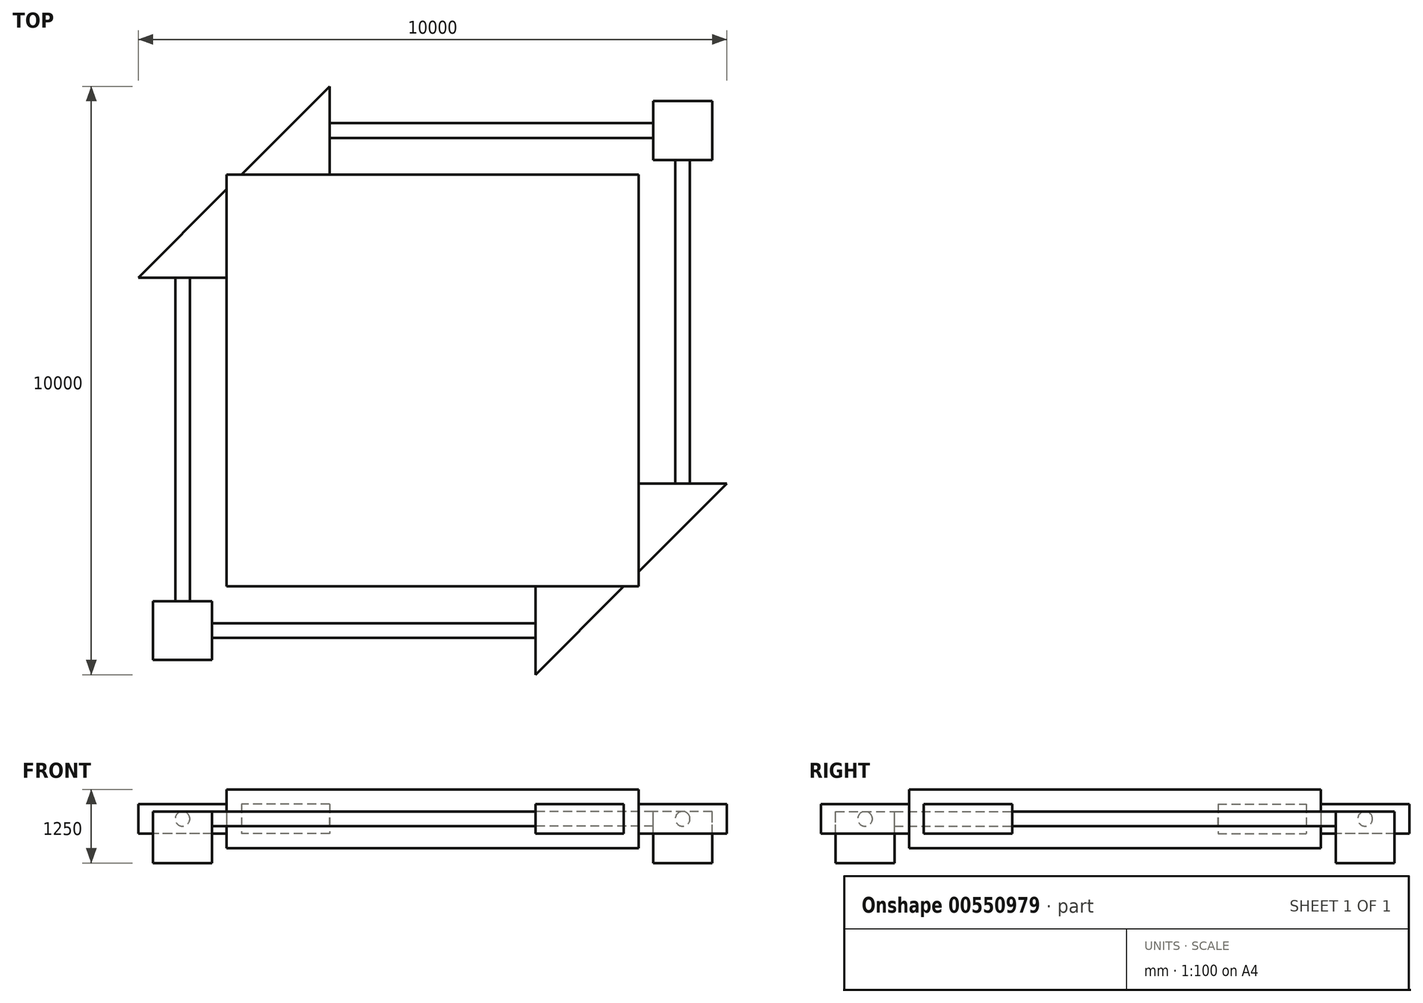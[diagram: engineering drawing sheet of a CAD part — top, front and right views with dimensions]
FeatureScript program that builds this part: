
annotation { "Feature Type Name" : "Feature", "Feature Type Description" : "" }
export const myFeature = defineFeature(function(context is Context, id is Id, definition is map)
    precondition{}
    {
        {
            var Q0;
            Q0=qCreatedBy(makeId("Top.planeOp"),FACE);
            var sketch = newSketch(context, id + "F0", { "sketchPlane" : qUnion([Q0])});
            skLineSegment(sketch, "E0.bottom", {"start": v(3500, -3500) * mm, "end": v(-3500, -3500) * mm});
            skLineSegment(sketch, "E0.top", {"start": v(3500, 3500) * mm, "end": v(-3500, 3500) * mm});
            skLineSegment(sketch, "E0.left", {"start": v(3500, -3500) * mm, "end": v(3500, 3500) * mm});
            skLineSegment(sketch, "E0.right", {"start": v(-3500, -3500) * mm, "end": v(-3500, 3500) * mm});
            skPoint(sketch, "E0.middle", {"position": v(0, 0) * mm});
            skLineSegment(sketch, "E1", {"start": v(0, 3500) * mm, "end": v(0, -3500) * mm, "construction": true});
            skLineSegment(sketch, "E2", {"start": v(-3500, 0) * mm, "end": v(3500, 0) * mm, "construction": true});
            skSolve(sketch);
        }
        {
            var Q0;
            Q0=makeQuery(id+"F0.imprint","IMPRINT",FACE,{"disambiguationData":[TD([[makeQuery(id+"F0.imprint","IMPRINT",EDGE,{"derivedFrom":sQuery(id+"F0.wireOp",EDGE,"E0.bottom")}),-1.0]])]});
            extrude(context, id + "F1", {"entities" : qUnion([Q0]), "depth" : 1000 * mm, "offsetDistance" : 25 * mm});
        }
        {
            var Q0;
            Q0=makeQuery(id+"F1.opExtrude","CAP_FACE",FACE,{"disambiguationData":[OSD([sQuery(id+"F0.wireOp",EDGE,"E0.bottom"),sQuery(id+"F0.wireOp",EDGE,"E0.top"),sQuery(id+"F0.wireOp",EDGE,"E0.left"),sQuery(id+"F0.wireOp",EDGE,"E0.right")])],"isStart":false});
            cPlane(context, id + "F2", {"entities" : qUnion([Q0]), "cplaneType" : CPlaneType.OFFSET, "offset" : 500 * mm, "oppositeDirection" : true, "width" : 150 * mm, "height" : 150 * mm});
        }
        {
            var Q0;
            Q0=qCreatedBy(id+"F2.planeOp",FACE);
            var sketch = newSketch(context, id + "F3", { "sketchPlane" : qUnion([Q0])});
            skLineSegment(sketch, "E3.0", {"start": v(3500, -3500) * mm, "end": v(-3500, -3500) * mm});
            skLineSegment(sketch, "E3.1", {"start": v(-3500, -3500) * mm, "end": v(-3500, 3500) * mm});
            skLineSegment(sketch, "E3.2", {"start": v(3500, 3500) * mm, "end": v(-3500, 3500) * mm});
            skLineSegment(sketch, "E3.3", {"start": v(3500, -3500) * mm, "end": v(3500, 3500) * mm});
            skLineSegment(sketch, "E4", {"start": v(-3500, 1750) * mm, "end": v(-5000, 1750) * mm});
            skLineSegment(sketch, "E5", {"start": v(-4250, 1750) * mm, "end": v(-4250, -4250) * mm});
            skLineSegment(sketch, "E6.bottom", {"start": v(-3750, -4750) * mm, "end": v(-4750, -4750) * mm});
            skLineSegment(sketch, "E6.top", {"start": v(-3750, -3750) * mm, "end": v(-4750, -3750) * mm});
            skLineSegment(sketch, "E6.left", {"start": v(-3750, -4750) * mm, "end": v(-3750, -3750) * mm});
            skLineSegment(sketch, "E6.right", {"start": v(-4750, -4750) * mm, "end": v(-4750, -3750) * mm});
            skPoint(sketch, "E6.middle", {"position": v(-4250, -4250) * mm});
            skPoint(sketch, "E7.orphan", {"position": v(-3500, 3250) * mm});
            skLineSegment(sketch, "E8", {"start": v(-1750, 5000) * mm, "end": v(-1750, 3500) * mm});
            skLineSegment(sketch, "E9", {"start": v(-3500, 3250) * mm, "end": v(-5000, 1750) * mm});
            skLineSegment(sketch, "E10", {"start": v(-1750, 5000) * mm, "end": v(-3250, 3500) * mm});
            skLineSegment(sketch, "E11", {"start": v(-1750, 4250) * mm, "end": v(4250, 4250) * mm});
            skLineSegment(sketch, "E12.bottom", {"start": v(4750, 3750) * mm, "end": v(3750, 3750) * mm});
            skLineSegment(sketch, "E12.top", {"start": v(4750, 4750) * mm, "end": v(3750, 4750) * mm});
            skLineSegment(sketch, "E12.left", {"start": v(4750, 3750) * mm, "end": v(4750, 4750) * mm});
            skLineSegment(sketch, "E12.right", {"start": v(3750, 3750) * mm, "end": v(3750, 4750) * mm});
            skPoint(sketch, "E12.middle", {"position": v(4250, 4250) * mm});
            skSolve(sketch);
        }
        {
            var Q0;
            {var subQ3=sQuery(id+"F3.wireOp",EDGE,"E9");Q0=makeQuery(id+"F3.imprint","IMPRINT",FACE,{"disambiguationData":[TD([[makeQuery(id+"F3.imprint","IMPRINT",EDGE,{"derivedFrom":subQ3}),1.0]])]});}
            var Q1;
            {var subQ3=sQuery(id+"F3.wireOp",EDGE,"E10");Q1=makeQuery(id+"F3.imprint","IMPRINT",FACE,{"disambiguationData":[TD([[makeQuery(id+"F3.imprint","IMPRINT",EDGE,{"derivedFrom":subQ3}),1.0]])]});}
            extrude(context, id + "F4", {"entities" : qUnion([Q0, Q1]), "endBound" : BoundingType.SYMMETRIC, "depth" : 500 * mm, "offsetDistance" : 25 * mm});
        }
        {
            var Q0;
            Q0=makeQuery(id+"F3.imprint","IMPRINT",FACE,{"disambiguationData":[TD([[makeQuery(id+"F3.imprint","IMPRINT",EDGE,{"derivedFrom":sQuery(id+"F3.wireOp",EDGE,"E6.bottom")}),-1.0]])]});
            var Q1;
            {var subQ1=sQuery(id+"F3.wireOp",EDGE,"E12.bottom");Q1=makeQuery(id+"F3.imprint","IMPRINT",FACE,{"disambiguationData":[TD([[makeQuery(id+"F3.imprint","IMPRINT",EDGE,{"derivedFrom":subQ1}),-1.0]])]});}
            var Q2;
            Q2=makeQuery(id+"F4.opExtrude","CAP_FACE",FACE,{"disambiguationData":[OSD([sQuery(id+"F3.wireOp",EDGE,"E3.1"),sQuery(id+"F3.wireOp",EDGE,"E4"),sQuery(id+"F3.wireOp",EDGE,"2qhpMPNh-2FLz-tSfa-bh7G-4xK9FkM5qJEm")])],"isStart":true});
            extrude(context, id + "F5", {"entities" : qUnion([Q0, Q1]), "operationType" : NewBodyOperationType.ADD, "oppositeDirection" : true, "depth" : 750 * mm, "endBoundEntityFace" : qUnion([Q2]), "offsetDistance" : 25 * mm, "hasSecondDirection" : true, "secondDirectionOppositeDirection" : false, "secondDirectionDepth" : 125 * mm});
        }
        {
            var Q0;
            Q0=makeQuery(id+"F4.opExtrude","SWEPT_FACE",FACE,{"disambiguationData":[OSD([sQuery(id+"F3.wireOp",EDGE,"E4")])]});
            var sketch = newSketch(context, id + "F6", { "sketchPlane" : qUnion([Q0])});
            skLineSegment(sketch, "E13", {"start": v(-4250, 750) * mm, "end": v(-4250, 500) * mm, "construction": true});
            skLineSegment(sketch, "E14", {"start": v(-3500, 500) * mm, "end": v(-2750, 500) * mm, "construction": true});
            skLineSegment(sketch, "E15", {"start": v(-4250, 500) * mm, "end": v(-4250, 250) * mm, "construction": true});
            skCircle(sketch, "E16", {"center": v(-4250, 500) * mm, "radius": 125 * mm});
            skSolve(sketch);
        }
        {
            var Q0;
            Q0=makeQuery(id+"F6.imprint","IMPRINT",FACE,{"disambiguationData":[TD([[makeQuery(id+"F6.imprint","IMPRINT",EDGE,{"derivedFrom":sQuery(id+"F6.wireOp",EDGE,"E16")}),1.0]])]});
            var Q1;
            Q1=sQuery(id+"F3.wireOp",VERTEX,"E6.top.end");
            extrude(context, id + "F7", {"entities" : qUnion([Q0]), "endBound" : BoundingType.UP_TO_VERTEX, "depth" : 10000 * mm, "endBoundEntityVertex" : qUnion([Q1]), "offsetDistance" : 25 * mm});
        }
        {
            var Q0;
            Q0=makeQuery(id+"F4.opExtrude","SWEPT_FACE",FACE,{"disambiguationData":[OSD([sQuery(id+"F3.wireOp",EDGE,"E8")])]});
            var sketch = newSketch(context, id + "F8", { "sketchPlane" : qUnion([Q0])});
            skLineSegment(sketch, "E17", {"start": v(4250, 750) * mm, "end": v(4250, 500) * mm, "construction": true});
            skLineSegment(sketch, "E18", {"start": v(5000, 500) * mm, "end": v(4250, 500) * mm, "construction": true});
            skLineSegment(sketch, "E19", {"start": v(4250, 500) * mm, "end": v(3500, 500) * mm, "construction": true});
            skLineSegment(sketch, "E20", {"start": v(4250, 500) * mm, "end": v(4250, 250) * mm, "construction": true});
            skCircle(sketch, "E21", {"center": v(4250, 500) * mm, "radius": 125 * mm});
            skSolve(sketch);
        }
        {
            var Q0;
            Q0 = qSketchRegion(id + "F8", true);
            var Q1;
            Q1=makeQuery(id+"F5.opExtrude","SWEPT_FACE",FACE,{"disambiguationData":[OSD([sQuery(id+"F3.wireOp",EDGE,"E12.right")])]});
            extrude(context, id + "F9", {"entities" : qUnion([Q0]), "endBound" : BoundingType.UP_TO_SURFACE, "depth" : 25 * mm, "endBoundEntityFace" : qUnion([Q1]), "offsetDistance" : 25 * mm});
        }
        {
            var Q0;
            Q0=qCreatedBy(makeId("Origin.pointOp"),VERTEX);
            var Q1;
            Q1=makeQuery(id+"F1.opExtrude","SWEPT_FACE",FACE,{"disambiguationData":[OSD([sQuery(id+"F0.wireOp",EDGE,"E0.bottom")])]});
            cPlane(context, id + "F10", {"entities" : qUnion([Q0, Q1]), "cplaneType" : CPlaneType.PLANE_POINT, "offset" : 25 * mm, "width" : 150 * mm, "height" : 150 * mm});
        }
        {
            var Q0;
            Q0=qCreatedBy(id+"F10.planeOp",FACE);
            var sketch = newSketch(context, id + "F11", { "sketchPlane" : qUnion([Q0])});
            skLineSegment(sketch, "E22", {"start": v(0, 0) * mm, "end": v(0, 1000) * mm, "construction": true});
            skSolve(sketch);
        }
        {
            var Q0;
            Q0=makeQuery(id+"F7.opExtrude","SWEPT_BODY",BODY,{"disambiguationData":[OSD([sQuery(id+"F6.wireOp",EDGE,"E16")])]});
            var Q1;
            Q1=makeQuery(id+"F4.opExtrude","SWEPT_BODY",BODY,{"disambiguationData":[OSD([sQuery(id+"F3.wireOp",EDGE,"E3.2"),sQuery(id+"F3.wireOp",EDGE,"E8"),sQuery(id+"F3.wireOp",EDGE,"E10")])]});
            var Q2;
            Q2=makeQuery(id+"F4.opExtrude","SWEPT_BODY",BODY,{"disambiguationData":[OSD([sQuery(id+"F3.wireOp",EDGE,"E3.1"),sQuery(id+"F3.wireOp",EDGE,"E4"),sQuery(id+"F3.wireOp",EDGE,"E9")])]});
            var Q3;
            Q3=makeQuery(id+"F9.opExtrude","SWEPT_BODY",BODY,{"disambiguationData":[OSD([sQuery(id+"F8.wireOp",EDGE,"E21")])]});
            var Q4;
            Q4=sQuery(id+"F11.wireOp",EDGE,"E22");
            circularPattern(context, id + "F12", {"entities" : qUnion([Q0, Q1, Q2, Q3]), "axis" : qUnion([Q4]), "angle" : 360 * degree, "instanceCount" : 2, "equalSpace" : true});
        }
    });
